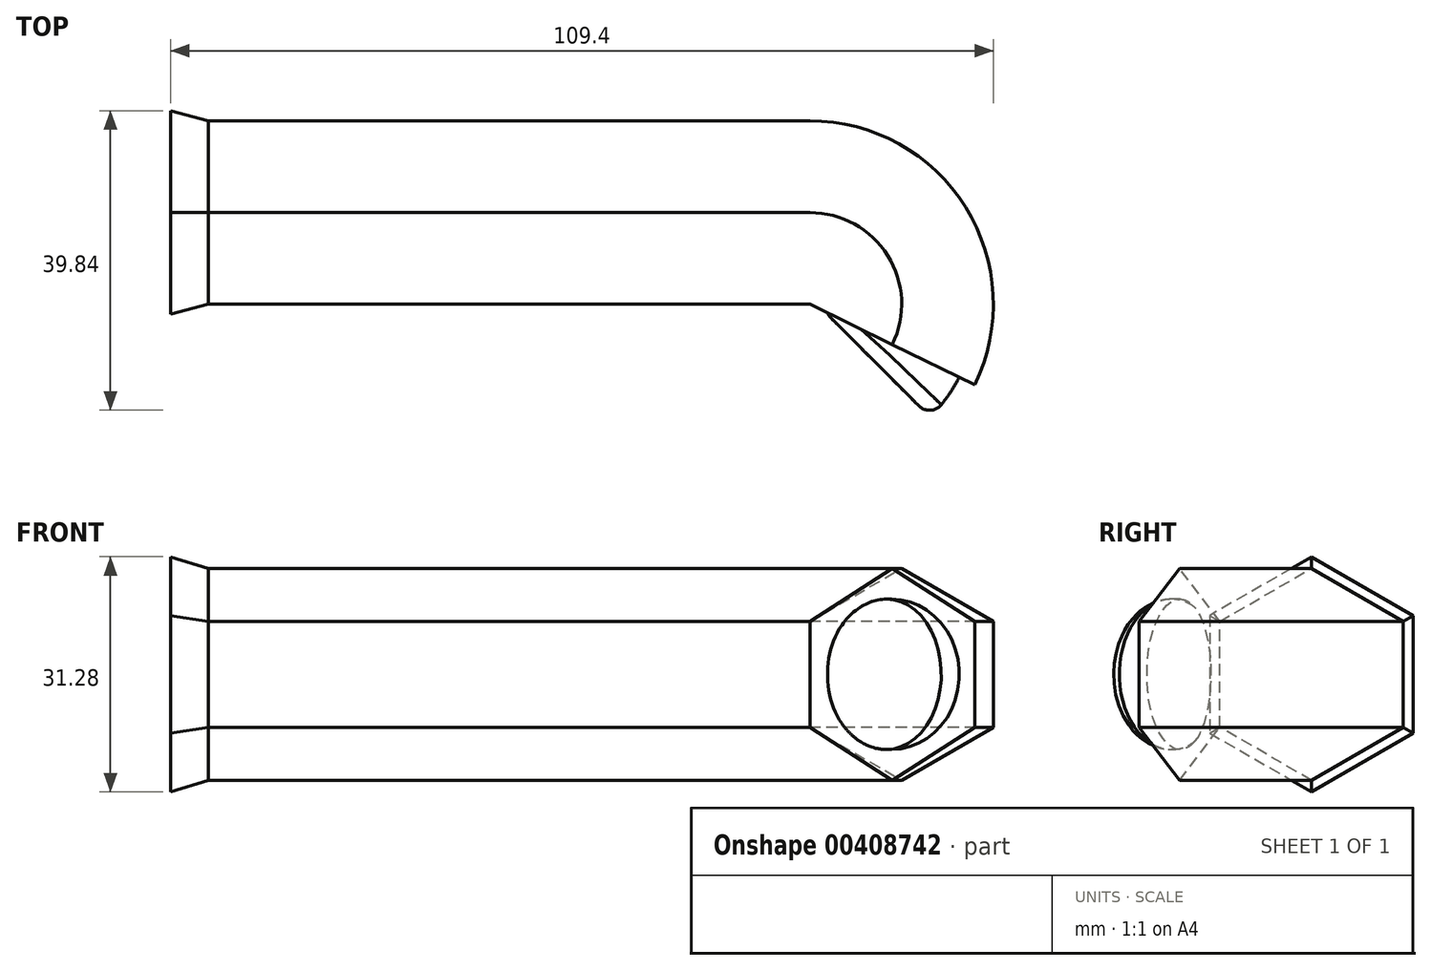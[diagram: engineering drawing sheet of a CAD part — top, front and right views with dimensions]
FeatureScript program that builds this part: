
annotation { "Feature Type Name" : "Feature", "Feature Type Description" : "" }
export const myFeature = defineFeature(function(context is Context, id is Id, definition is map)
    precondition{}
    {
        {
            var Q0;
            Q0=qCreatedBy(makeId("Front.planeOp"),FACE);
            var sketch = newSketch(context, id + "F0", { "sketchPlane" : qUnion([Q0])});
            skCircle(sketch, "E0", {"center": v(0, 0) * mm, "radius": 10 * mm});
            skSolve(sketch);
        }
        {
            var Q0;
            Q0=qCreatedBy(makeId("Front.planeOp"),FACE);
            var sketch = newSketch(context, id + "F1", { "sketchPlane" : qUnion([Q0])});
            skLineSegment(sketch, "E1", {"start": v(-11.22, 5.1) * mm, "end": v(-11.22, -6.84) * mm});
            skSolve(sketch);
        }
        {
            var Q0;
            Q0=makeQuery(id+"F0.imprint","IMPRINT",FACE,{"disambiguationData":[TD([[makeQuery(id+"F0.imprint","IMPRINT",EDGE,{"derivedFrom":sQuery(id+"F0.wireOp",EDGE,"E0")}),1.0]])]});
            var Q1;
            Q1=sQuery(id+"F1.wireOp",EDGE,"E1");
            revolve(context, id + "F2", {"entities" : qUnion([Q0]), "axis" : qUnion([Q1]), "revolveType" : RevolveType.ONE_DIRECTION, "angle" : 45 * degree});
        }
        {
            var Q0;
            Q0=qCreatedBy(makeId("Front.planeOp"),FACE);
            var sketch = newSketch(context, id + "F3", { "sketchPlane" : qUnion([Q0])});
            skCircle(sketch, "E2.cCircle", {"center": v(0, 0) * mm, "radius": 12.2 * mm, "construction": true});
            skLineSegment(sketch, "E2.0", {"start": v(12.2, 7.04) * mm, "end": v(12.2, -7.04) * mm});
            skLineSegment(sketch, "E2.1", {"start": v(12.2, -7.04) * mm, "end": v(0, -14.09) * mm});
            skLineSegment(sketch, "E2.2", {"start": v(0, -14.09) * mm, "end": v(-12.2, -7.04) * mm});
            skLineSegment(sketch, "E2.3", {"start": v(-12.2, -7.04) * mm, "end": v(-12.2, 7.04) * mm});
            skLineSegment(sketch, "E2.4", {"start": v(-12.2, 7.04) * mm, "end": v(0, 14.09) * mm});
            skLineSegment(sketch, "E2.5", {"start": v(0, 14.09) * mm, "end": v(12.2, 7.04) * mm});
            skPoint(sketch, "E2.0.midPoint", {"position": v(12.2, 0) * mm});
            skSolve(sketch);
        }
        {
            var Q0;
            Q0=makeQuery(id+"F3.imprint","IMPRINT",FACE,{"disambiguationData":[TD([[makeQuery(id+"F3.imprint","IMPRINT",EDGE,{"derivedFrom":sQuery(id+"F3.wireOp",EDGE,"E2.0")}),-1.0]])]});
            var Q1;
            Q1=sQuery(id+"F3.wireOp",EDGE,"E2.3");
            revolve(context, id + "F4", {"operationType" : NewBodyOperationType.ADD, "entities" : qUnion([Q0]), "axis" : qUnion([Q1]), "revolveType" : RevolveType.TWO_DIRECTIONS, "oppositeDirection" : true, "angle" : 26 * degree, "angleBack" : 270 * degree});
        }
        {
            var Q0;
            Q0=makeQuery(id+"F4.opRevolve","CAP_FACE",FACE,{"disambiguationData":[OSD([sQuery(id+"F3.wireOp",EDGE,"E2.0"),sQuery(id+"F3.wireOp",EDGE,"E2.1"),sQuery(id+"F3.wireOp",EDGE,"E2.2"),sQuery(id+"F3.wireOp",EDGE,"E2.3"),sQuery(id+"F3.wireOp",EDGE,"E2.4"),sQuery(id+"F3.wireOp",EDGE,"E2.5")])],"isStart":true});
            extrude(context, id + "F5", {"entities" : qUnion([Q0]), "operationType" : NewBodyOperationType.ADD, "depth" : 80 * mm});
        }
        {
            var Q0;
            Q0=makeQuery(id+"F5.opExtrude","CAP_FACE",FACE,{"disambiguationData":[OSD([sQuery(id+"F3.wireOp",EDGE,"E2.0"),sQuery(id+"F3.wireOp",EDGE,"E2.1"),sQuery(id+"F3.wireOp",EDGE,"E2.2"),sQuery(id+"F3.wireOp",EDGE,"E2.3"),sQuery(id+"F3.wireOp",EDGE,"E2.4"),sQuery(id+"F3.wireOp",EDGE,"E2.5")])],"isStart":false});
            extrude(context, id + "F6", {"entities" : qUnion([Q0]), "operationType" : NewBodyOperationType.ADD, "depth" : 5 * mm, "hasDraft" : true, "draftAngle" : 15 * degree});
        }
        {
            var Q0;
            Q0=makeQuery(id+"F2.opRevolve","CAP_EDGE",EDGE,{"disambiguationData":[OSD([sQuery(id+"F0.wireOp",EDGE,"E0")])],"isStart":false});
            fillet(context, id + "F7", {"entities" : qUnion([Q0]), "radius" : 2 * mm, "tangentPropagation" : true, "allowEdgeOverflow" : false});
        }
    });
